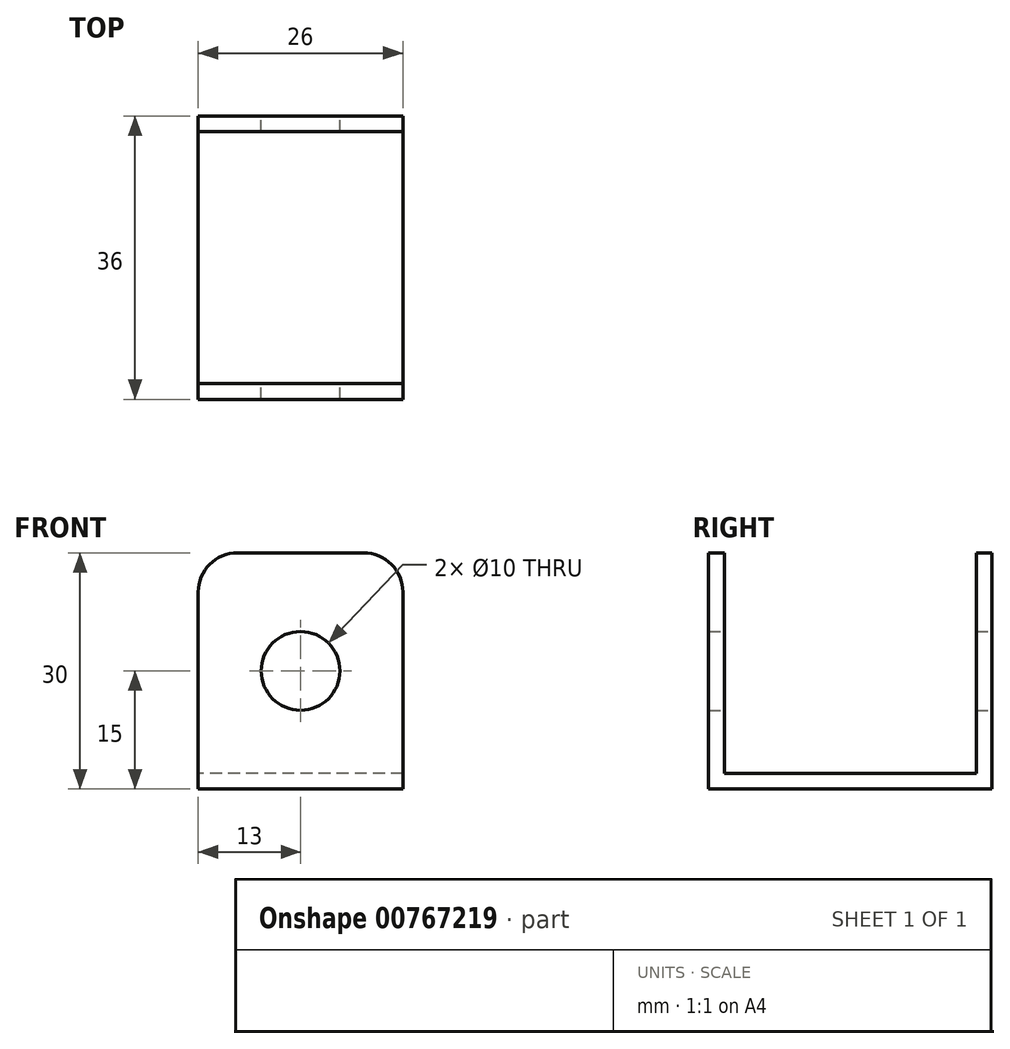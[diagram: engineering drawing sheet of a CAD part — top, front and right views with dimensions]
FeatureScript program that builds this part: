
annotation { "Feature Type Name" : "Feature", "Feature Type Description" : "" }
export const myFeature = defineFeature(function(context is Context, id is Id, definition is map)
    precondition{}
    {
        {
            var Q0;
            Q0=qCreatedBy(makeId("Right.planeOp"),FACE);
            var sketch = newSketch(context, id + "F0", { "sketchPlane" : qUnion([Q0])});
            skLineSegment(sketch, "E0.bottom", {"start": v(-18, 15) * mm, "end": v(-16, 15) * mm});
            skLineSegment(sketch, "E0.top", {"start": v(-18, -15) * mm, "end": v(18, -15) * mm});
            skLineSegment(sketch, "E0.left", {"start": v(-18, 15) * mm, "end": v(-18, -15) * mm});
            skLineSegment(sketch, "E0.right", {"start": v(18, 15) * mm, "end": v(18, -15) * mm});
            skPoint(sketch, "E0.middle", {"position": v(0, 0) * mm});
            skLineSegment(sketch, "E1.top", {"start": v(-16, -13) * mm, "end": v(16, -13) * mm});
            skLineSegment(sketch, "E1.left", {"start": v(-16, 15) * mm, "end": v(-16, -13) * mm});
            skLineSegment(sketch, "E1.right", {"start": v(16, 15) * mm, "end": v(16, -13) * mm});
            skLineSegment(sketch, "E2.trimOffspring", {"start": v(16, 15) * mm, "end": v(18, 15) * mm});
            skSolve(sketch);
        }
        {
            var Q0;
            Q0 = qSketchRegion(id + "F0", true);
            extrude(context, id + "F1", {"entities" : qUnion([Q0]), "endBound" : BoundingType.SYMMETRIC, "depth" : 26 * mm, "offsetDistance" : 25 * mm});
        }
        {
            var Q0;
            Q0=qCreatedBy(makeId("Front.planeOp"),FACE);
            var sketch = newSketch(context, id + "F2", { "sketchPlane" : qUnion([Q0])});
            skCircle(sketch, "E3", {"center": v(0, 0) * mm, "radius": 5 * mm});
            skSolve(sketch);
        }
        {
            var Q0;
            Q0 = qSketchRegion(id + "F2", true);
            extrude(context, id + "F3", {"entities" : qUnion([Q0]), "operationType" : NewBodyOperationType.REMOVE, "endBound" : BoundingType.SYMMETRIC, "depth" : 1000 * mm, "offsetDistance" : 25 * mm});
        }
        {
            var Q0;
            Q0=makeQuery(id+"F1.opExtrude","CAP_EDGE",EDGE,{"disambiguationData":[OSD([sQuery(id+"F0.wireOp",EDGE,"E2.trimOffspring")])],"isStart":false});
            var Q1;
            Q1=makeQuery(id+"F1.opExtrude","CAP_EDGE",EDGE,{"disambiguationData":[OSD([sQuery(id+"F0.wireOp",EDGE,"E2.trimOffspring")])],"isStart":true});
            var Q2;
            Q2=makeQuery(id+"F1.opExtrude","CAP_EDGE",EDGE,{"disambiguationData":[OSD([sQuery(id+"F0.wireOp",EDGE,"E0.bottom")])],"isStart":true});
            var Q3;
            Q3=makeQuery(id+"F1.opExtrude","CAP_EDGE",EDGE,{"disambiguationData":[OSD([sQuery(id+"F0.wireOp",EDGE,"E0.bottom")])],"isStart":false});
            fillet(context, id + "F4", {"entities" : qUnion([Q0, Q1, Q2, Q3]), "radius" : 5 * mm, "tangentPropagation" : true, "allowEdgeOverflow" : false});
        }
    });
